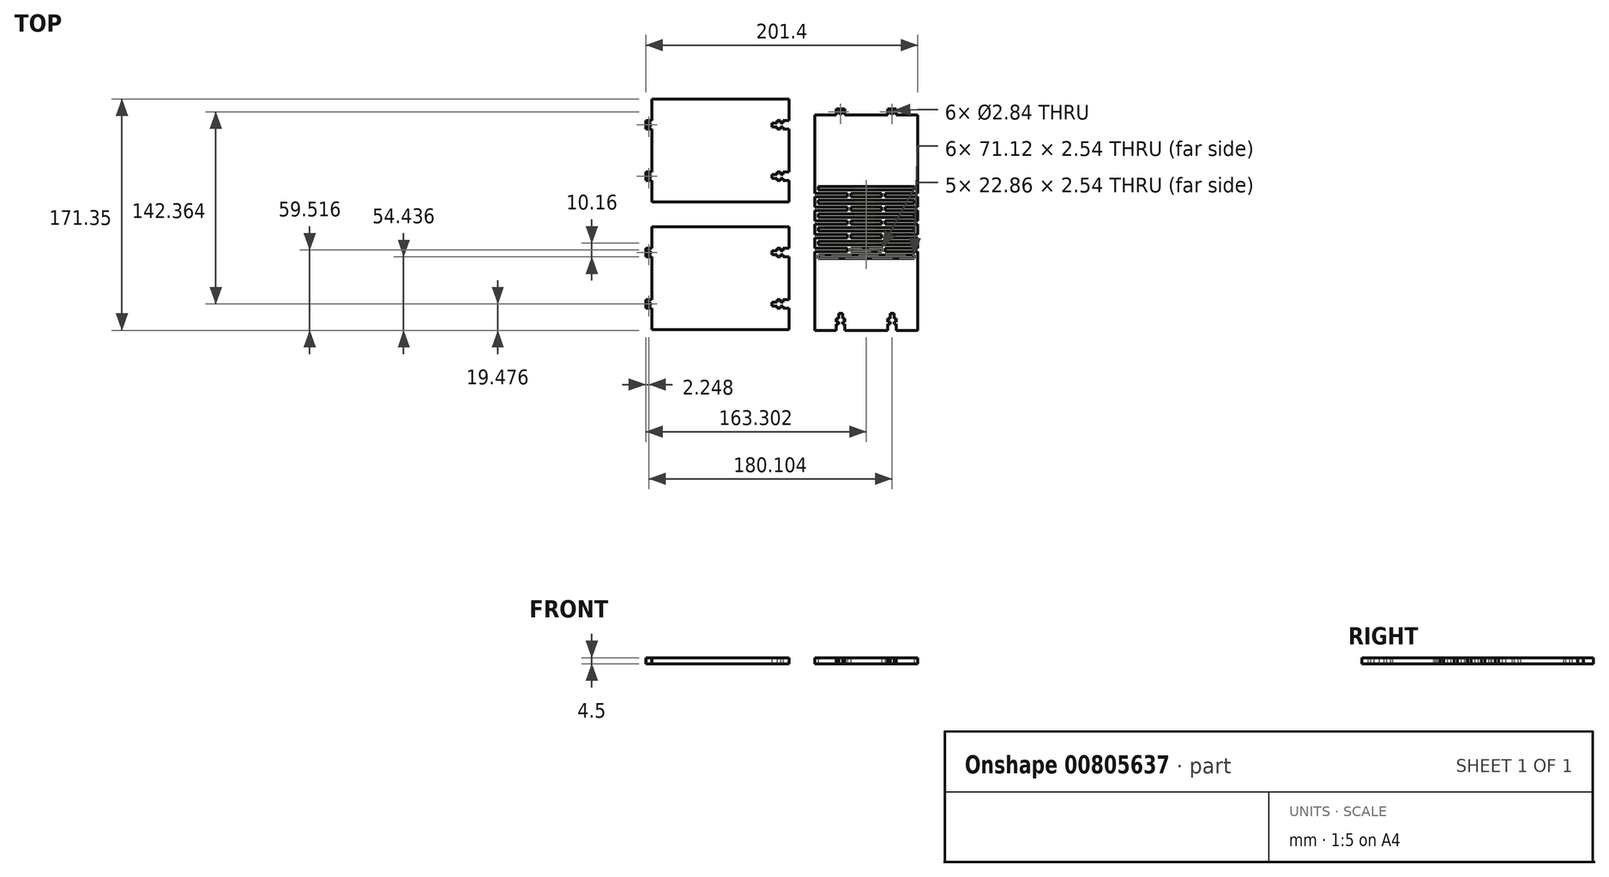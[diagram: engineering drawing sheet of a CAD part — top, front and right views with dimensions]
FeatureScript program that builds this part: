
annotation { "Feature Type Name" : "Feature", "Feature Type Description" : "" }
export const myFeature = defineFeature(function(context is Context, id is Id, definition is map)
    precondition{}
    {
        {
            var Q0;
            Q0=qCreatedBy(makeId("Top.planeOp"),FACE);
            var sketch = newSketch(context, id + "F0", { "sketchPlane" : qUnion([Q0])});
            skLineSegment(sketch, "E0.bottom", {"start": v(-89.07, 43.47) * mm, "end": v(12.53, 43.47) * mm});
            skLineSegment(sketch, "E0.top", {"start": v(-89.07, -32.73) * mm, "end": v(12.53, -32.73) * mm});
            skLineSegment(sketch, "E0.right", {"start": v(12.53, 43.47) * mm, "end": v(12.53, 27.6) * mm});
            skLineSegment(sketch, "E1.bottom", {"start": v(31.63, 31.71) * mm, "end": v(47.5, 31.71) * mm});
            skLineSegment(sketch, "E1.left", {"start": v(31.63, 31.71) * mm, "end": v(31.63, -26.45) * mm});
            skLineSegment(sketch, "E1.right", {"start": v(107.83, 31.71) * mm, "end": v(107.83, -26.45) * mm});
            skLineSegment(sketch, "E2", {"start": v(12.53, -32.73) * mm, "end": v(12.53, -16.86) * mm});
            skLineSegment(sketch, "E3.bottom", {"start": v(6.18, 27.6) * mm, "end": v(3.8, 27.6) * mm});
            skLineSegment(sketch, "E3.top", {"start": v(6.18, 21.24) * mm, "end": v(3.8, 21.24) * mm});
            skLineSegment(sketch, "E3.left", {"start": v(6.18, 27.6) * mm, "end": v(6.18, 25.84) * mm});
            skLineSegment(sketch, "E3.right", {"start": v(3.8, 27.6) * mm, "end": v(3.8, 25.84) * mm});
            skLineSegment(sketch, "E4.0", {"start": v(3.8, 25.84) * mm, "end": v(-0.17, 25.84) * mm});
            skLineSegment(sketch, "E5.0", {"start": v(3.8, 23) * mm, "end": v(-0.17, 23) * mm});
            skLineSegment(sketch, "E6", {"start": v(-0.17, 25.84) * mm, "end": v(-0.17, 23) * mm});
            skPoint(sketch, "E7.start.orphan", {"position": v(6.18, 24.42) * mm});
            skLineSegment(sketch, "E8.trimOffspring", {"start": v(6.18, 23) * mm, "end": v(6.18, 21.24) * mm});
            skLineSegment(sketch, "E9.trimOffspring", {"start": v(3.8, 23) * mm, "end": v(3.8, 21.24) * mm});
            skLineSegment(sketch, "E10", {"start": v(-89.07, 43.47) * mm, "end": v(-89.07, 27.6) * mm});
            skLineSegment(sketch, "E11.0", {"start": v(-89.07, 27.6) * mm, "end": v(-93.57, 27.6) * mm});
            skLineSegment(sketch, "E12.0", {"start": v(-89.07, 21.24) * mm, "end": v(-93.57, 21.24) * mm});
            skLineSegment(sketch, "E13", {"start": v(-93.57, 27.6) * mm, "end": v(-93.57, 21.24) * mm});
            skLineSegment(sketch, "E14.trimOffspring", {"start": v(-89.07, 21.24) * mm, "end": v(-89.07, -10.51) * mm});
            skLineSegment(sketch, "E15.0", {"start": v(12.53, 21.24) * mm, "end": v(7.95, 21.24) * mm});
            skLineSegment(sketch, "E16.0", {"start": v(12.53, 27.6) * mm, "end": v(7.95, 27.6) * mm});
            skLineSegment(sketch, "E17", {"start": v(7.95, 27.6) * mm, "end": v(7.95, 25.84) * mm});
            skLineSegment(sketch, "E18", {"start": v(6.18, 23) * mm, "end": v(7.95, 23) * mm});
            skLineSegment(sketch, "E19", {"start": v(6.18, 25.84) * mm, "end": v(7.95, 25.84) * mm});
            skLineSegment(sketch, "E20.trimOffspring", {"start": v(7.95, 23) * mm, "end": v(7.95, 21.24) * mm});
            skLineSegment(sketch, "E21.MirrorCS", {"start": v(6.18, -16.86) * mm, "end": v(3.8, -16.86) * mm});
            skLineSegment(sketch, "E22.MirrorCS", {"start": v(6.18, -12.26) * mm, "end": v(7.95, -12.26) * mm});
            skLineSegment(sketch, "E23.MirrorCS", {"start": v(6.18, -10.5) * mm, "end": v(3.8, -10.5) * mm});
            skLineSegment(sketch, "E24.MirrorCS", {"start": v(6.18, -15.1) * mm, "end": v(7.95, -15.1) * mm});
            skLineSegment(sketch, "E25.MirrorCS", {"start": v(6.18, -16.86) * mm, "end": v(6.18, -15.1) * mm});
            skLineSegment(sketch, "E26.MirrorCS", {"start": v(7.95, -12.26) * mm, "end": v(7.95, -10.5) * mm});
            skLineSegment(sketch, "E27.MirrorCS", {"start": v(7.95, -16.86) * mm, "end": v(7.95, -15.1) * mm});
            skLineSegment(sketch, "E28.MirrorCS", {"start": v(6.18, -12.26) * mm, "end": v(6.18, -10.5) * mm});
            skLineSegment(sketch, "E29.MirrorCS", {"start": v(3.8, -12.26) * mm, "end": v(3.8, -10.5) * mm});
            skLineSegment(sketch, "E30.MirrorCS", {"start": v(-0.17, -15.1) * mm, "end": v(-0.17, -12.26) * mm});
            skLineSegment(sketch, "E31.MirrorCS", {"start": v(3.8, -15.1) * mm, "end": v(-0.17, -15.1) * mm});
            skLineSegment(sketch, "E32.MirrorCS", {"start": v(3.8, -12.26) * mm, "end": v(-0.17, -12.26) * mm});
            skLineSegment(sketch, "E33.MirrorCS", {"start": v(3.8, -16.86) * mm, "end": v(3.8, -15.1) * mm});
            skLineSegment(sketch, "E34.MirrorCS", {"start": v(-89.07, -10.51) * mm, "end": v(-93.57, -10.51) * mm});
            skPoint(sketch, "E35.MirrorP", {"position": v(6.18, -13.68) * mm});
            skLineSegment(sketch, "E36.MirrorCS", {"start": v(12.53, -16.86) * mm, "end": v(7.95, -16.86) * mm});
            skLineSegment(sketch, "E37.MirrorCS", {"start": v(-89.07, -16.86) * mm, "end": v(-93.57, -16.86) * mm});
            skLineSegment(sketch, "E38.MirrorCS", {"start": v(12.53, -10.5) * mm, "end": v(7.95, -10.5) * mm});
            skLineSegment(sketch, "E39.MirrorCS", {"start": v(-93.57, -16.86) * mm, "end": v(-93.57, -10.51) * mm});
            skLineSegment(sketch, "E40.trimOffspring", {"start": v(12.53, 21.24) * mm, "end": v(12.53, -10.5) * mm});
            skLineSegment(sketch, "E41.trimOffspring", {"start": v(12.53, -16.86) * mm, "end": v(12.53, -32.73) * mm});
            skLineSegment(sketch, "E42.trimOffspring", {"start": v(-89.07, -16.86) * mm, "end": v(-89.07, -32.73) * mm});
            skPoint(sketch, "E43.start.orphan", {"position": v(12.53, 5.37) * mm});
            skPoint(sketch, "E44.MirrorCS.start.orphan", {"position": v(12.53, -127.45) * mm});
            skPoint(sketch, "E45.MirrorCS.end.orphan", {"position": v(12.53, -51.25) * mm});
            skPoint(sketch, "E46.MirrorCS.end.orphan", {"position": v(-89.07, -51.25) * mm});
            skPoint(sketch, "E46.MirrorCS.start.orphan", {"position": v(-89.07, -127.45) * mm});
            skLineSegment(sketch, "E47.MirrorCS", {"start": v(7.95, -71.72) * mm, "end": v(7.95, -73.48) * mm});
            skLineSegment(sketch, "E48.MirrorCS", {"start": v(6.18, -106.98) * mm, "end": v(7.95, -106.98) * mm});
            skLineSegment(sketch, "E49.MirrorCS", {"start": v(7.95, -106.98) * mm, "end": v(7.95, -105.22) * mm});
            skLineSegment(sketch, "E50.MirrorCS", {"start": v(6.18, -71.72) * mm, "end": v(7.95, -71.72) * mm});
            skLineSegment(sketch, "E51.MirrorCS", {"start": v(3.8, -106.98) * mm, "end": v(3.8, -105.23) * mm});
            skLineSegment(sketch, "E52.MirrorCS", {"start": v(6.18, -105.23) * mm, "end": v(3.8, -105.23) * mm});
            skLineSegment(sketch, "E53.MirrorCS", {"start": v(3.8, -71.72) * mm, "end": v(3.8, -73.48) * mm});
            skLineSegment(sketch, "E54.MirrorCS", {"start": v(6.18, -73.48) * mm, "end": v(3.8, -73.48) * mm});
            skLineSegment(sketch, "E55.MirrorCS", {"start": v(6.18, -71.72) * mm, "end": v(6.18, -73.48) * mm});
            skLineSegment(sketch, "E56.MirrorCS", {"start": v(6.18, -106.98) * mm, "end": v(6.18, -105.23) * mm});
            skLineSegment(sketch, "E57.MirrorCS", {"start": v(3.8, -67.13) * mm, "end": v(3.8, -68.88) * mm});
            skLineSegment(sketch, "E58.MirrorCS", {"start": v(7.95, -111.58) * mm, "end": v(7.95, -109.82) * mm});
            skLineSegment(sketch, "E59.MirrorCS", {"start": v(3.8, -111.58) * mm, "end": v(3.8, -109.82) * mm});
            skLineSegment(sketch, "E60.MirrorCS", {"start": v(6.18, -111.58) * mm, "end": v(3.8, -111.58) * mm});
            skLineSegment(sketch, "E61.MirrorCS", {"start": v(6.18, -67.13) * mm, "end": v(6.18, -68.88) * mm});
            skLineSegment(sketch, "E62.MirrorCS", {"start": v(6.18, -67.13) * mm, "end": v(3.8, -67.13) * mm});
            skLineSegment(sketch, "E63.MirrorCS", {"start": v(12.53, -67.12) * mm, "end": v(7.95, -67.12) * mm});
            skLineSegment(sketch, "E64.MirrorCS", {"start": v(6.18, -109.82) * mm, "end": v(7.95, -109.82) * mm});
            skLineSegment(sketch, "E65.MirrorCS", {"start": v(6.18, -111.58) * mm, "end": v(6.18, -109.82) * mm});
            skLineSegment(sketch, "E66.MirrorCS", {"start": v(7.95, -67.12) * mm, "end": v(7.95, -68.88) * mm});
            skLineSegment(sketch, "E67.MirrorCS", {"start": v(6.18, -68.88) * mm, "end": v(7.95, -68.88) * mm});
            skLineSegment(sketch, "E68.MirrorCS", {"start": v(3.8, -109.82) * mm, "end": v(-0.17, -109.82) * mm});
            skLineSegment(sketch, "E69.MirrorCS", {"start": v(3.8, -106.98) * mm, "end": v(-0.17, -106.98) * mm});
            skLineSegment(sketch, "E70.MirrorCS", {"start": v(-89.07, -73.47) * mm, "end": v(-93.57, -73.47) * mm});
            skLineSegment(sketch, "E71.MirrorCS", {"start": v(-93.57, -111.58) * mm, "end": v(-93.57, -105.23) * mm});
            skLineSegment(sketch, "E72.MirrorCS", {"start": v(-93.57, -67.12) * mm, "end": v(-93.57, -73.47) * mm});
            skLineSegment(sketch, "E73.MirrorCS", {"start": v(12.53, -111.58) * mm, "end": v(7.95, -111.58) * mm});
            skLineSegment(sketch, "E74.MirrorCS", {"start": v(3.8, -71.72) * mm, "end": v(-0.17, -71.72) * mm});
            skLineSegment(sketch, "E75.MirrorCS", {"start": v(3.8, -68.88) * mm, "end": v(-0.17, -68.88) * mm});
            skLineSegment(sketch, "E76.MirrorCS", {"start": v(12.53, -105.22) * mm, "end": v(7.95, -105.22) * mm});
            skLineSegment(sketch, "E77.MirrorCS", {"start": v(-89.07, -105.23) * mm, "end": v(-93.57, -105.23) * mm});
            skLineSegment(sketch, "E78.MirrorCS", {"start": v(12.53, -73.48) * mm, "end": v(7.95, -73.48) * mm});
            skLineSegment(sketch, "E79.MirrorCS", {"start": v(-89.07, -67.12) * mm, "end": v(-93.57, -67.12) * mm});
            skLineSegment(sketch, "E80.MirrorCS", {"start": v(-0.17, -68.88) * mm, "end": v(-0.17, -71.72) * mm});
            skLineSegment(sketch, "E81.MirrorCS", {"start": v(-0.17, -109.82) * mm, "end": v(-0.17, -106.98) * mm});
            skLineSegment(sketch, "E82.MirrorCS", {"start": v(-89.07, -111.58) * mm, "end": v(-93.57, -111.58) * mm});
            skLineSegment(sketch, "E83.MirrorCS", {"start": v(12.53, -127.45) * mm, "end": v(12.53, -111.58) * mm});
            skLineSegment(sketch, "E84.MirrorCS", {"start": v(12.53, -51.25) * mm, "end": v(12.53, -67.12) * mm});
            skLineSegment(sketch, "E85.MirrorCS", {"start": v(-89.07, -127.45) * mm, "end": v(-89.07, -111.58) * mm});
            skLineSegment(sketch, "E86.MirrorCS", {"start": v(-89.07, -127.45) * mm, "end": v(12.53, -127.45) * mm});
            skLineSegment(sketch, "E87.MirrorCS", {"start": v(-89.07, -51.25) * mm, "end": v(12.53, -51.25) * mm});
            skPoint(sketch, "E88.MirrorP", {"position": v(6.18, -108.4) * mm});
            skLineSegment(sketch, "E89.MirrorCS", {"start": v(-89.07, -67.12) * mm, "end": v(-89.07, -51.25) * mm});
            skLineSegment(sketch, "E90.MirrorCS", {"start": v(-89.07, -105.23) * mm, "end": v(-89.07, -73.47) * mm});
            skPoint(sketch, "E91.MirrorP", {"position": v(6.18, -70.3) * mm});
            skLineSegment(sketch, "E92.MirrorCS", {"start": v(12.53, -105.22) * mm, "end": v(12.53, -73.48) * mm});
            skLineSegment(sketch, "E93.MirrorCS", {"start": v(12.53, -67.12) * mm, "end": v(12.53, -51.25) * mm});
            skPoint(sketch, "E94.MirrorP", {"position": v(12.53, -89.35) * mm});
            skCircle(sketch, "E95", {"center": v(-91.32, 24.42) * mm, "radius": 1.42 * mm});
            skPoint(sketch, "E95.centerSnap0", {"position": v(-91.32, 27.6) * mm});
            skPoint(sketch, "E95.centerSnap1", {"position": v(-93.57, 24.42) * mm});
            skCircle(sketch, "E96.MirrorC", {"center": v(-91.32, -13.69) * mm, "radius": 1.42 * mm});
            skCircle(sketch, "E97.MirrorC", {"center": v(-91.32, -108.4) * mm, "radius": 1.42 * mm});
            skCircle(sketch, "E98.MirrorC", {"center": v(-91.32, -70.3) * mm, "radius": 1.42 * mm});
            skLineSegment(sketch, "E99", {"start": v(53.86, 31.71) * mm, "end": v(85.6, 31.71) * mm});
            skLineSegment(sketch, "E100.top", {"start": v(47.5, 36.2) * mm, "end": v(53.86, 36.2) * mm});
            skLineSegment(sketch, "E100.left", {"start": v(47.5, 31.71) * mm, "end": v(47.5, 36.2) * mm});
            skLineSegment(sketch, "E100.right", {"start": v(53.86, 31.71) * mm, "end": v(53.86, 36.2) * mm});
            skLineSegment(sketch, "E101.MirrorCS", {"start": v(91.96, 36.2) * mm, "end": v(85.6, 36.2) * mm});
            skLineSegment(sketch, "E102.MirrorCS", {"start": v(91.96, 31.71) * mm, "end": v(91.96, 36.2) * mm});
            skLineSegment(sketch, "E103.MirrorCS", {"start": v(85.6, 31.71) * mm, "end": v(85.6, 36.2) * mm});
            skCircle(sketch, "E104", {"center": v(50.68, 33.96) * mm, "radius": 1.42 * mm});
            skPoint(sketch, "E104.centerSnap0", {"position": v(50.68, 36.2) * mm});
            skPoint(sketch, "E105.start.orphan", {"position": v(47.5, 33.96) * mm});
            skPoint(sketch, "E106.trimOffspring.end.orphan", {"position": v(53.86, 33.96) * mm});
            skPoint(sketch, "E107.orphan", {"position": v(50.68, 31.71) * mm});
            skLineSegment(sketch, "E108.trimOffspring", {"start": v(91.96, 31.71) * mm, "end": v(107.83, 31.71) * mm});
            skPoint(sketch, "E109.end.orphan", {"position": v(69.73, 31.71) * mm});
            skPoint(sketch, "E110.end.orphan", {"position": v(-89.07, 5.37) * mm});
            skLineSegment(sketch, "E111", {"start": v(31.63, 31.71) * mm, "end": v(31.63, -21.37) * mm});
            skLineSegment(sketch, "E112", {"start": v(34.17, -21.37) * mm, "end": v(69.73, -21.37) * mm});
            skLineSegment(sketch, "E113", {"start": v(69.73, 31.71) * mm, "end": v(69.73, -127.88) * mm});
            skLineSegment(sketch, "E114.0", {"start": v(34.17, -23.91) * mm, "end": v(55.76, -23.91) * mm});
            skLineSegment(sketch, "E115.0", {"start": v(31.63, -26.45) * mm, "end": v(55.76, -26.45) * mm});
            skLineSegment(sketch, "E116", {"start": v(34.17, -21.37) * mm, "end": v(34.17, -23.91) * mm});
            skPoint(sketch, "E117.orphan", {"position": v(31.63, -23.91) * mm});
            skLineSegment(sketch, "E118.trimOffspring", {"start": v(55.87, -23.91) * mm, "end": v(69.73, -23.91) * mm});
            skLineSegment(sketch, "E119.trimOffspring", {"start": v(58.3, -26.45) * mm, "end": v(69.73, -26.45) * mm});
            skLineSegment(sketch, "E120.MirrorCS", {"start": v(107.83, 31.71) * mm, "end": v(107.83, -21.37) * mm});
            skPoint(sketch, "E121.MirrorP", {"position": v(107.83, -23.91) * mm});
            skLineSegment(sketch, "E122.0", {"start": v(31.63, -29) * mm, "end": v(55.76, -29) * mm});
            skLineSegment(sketch, "E123", {"start": v(58.3, -29) * mm, "end": v(69.73, -29) * mm});
            skLineSegment(sketch, "E124", {"start": v(55.76, -23.91) * mm, "end": v(55.87, -23.91) * mm});
            skLineSegment(sketch, "E125", {"start": v(55.76, -26.45) * mm, "end": v(55.76, -29) * mm});
            skLineSegment(sketch, "E126", {"start": v(58.3, -26.45) * mm, "end": v(58.3, -29) * mm});
            skLineSegment(sketch, "E127.trimOffspring", {"start": v(31.63, -29) * mm, "end": v(31.63, -36.61) * mm});
            skPoint(sketch, "E128.MirrorCS.end.orphan", {"position": v(69.73, -26.45) * mm});
            skPoint(sketch, "E129.MirrorCS.end.orphan", {"position": v(69.73, -23.91) * mm});
            skPoint(sketch, "E130.MirrorCS.end.orphan", {"position": v(81.16, -26.45) * mm});
            skPoint(sketch, "E130.MirrorCS.start.orphan", {"position": v(83.6, -23.91) * mm});
            skPoint(sketch, "E131.MirrorCS.end.orphan", {"position": v(83.7, -26.45) * mm});
            skPoint(sketch, "E131.MirrorCS.start.orphan", {"position": v(107.83, -26.45) * mm});
            skPoint(sketch, "E132.MirrorCS.end.orphan", {"position": v(83.7, -23.91) * mm});
            skPoint(sketch, "E133.MirrorCS.end.orphan", {"position": v(69.73, -21.37) * mm});
            skPoint(sketch, "E134.MirrorCS.end.orphan", {"position": v(105.3, -23.91) * mm});
            skPoint(sketch, "E134.MirrorCS.start.orphan", {"position": v(105.3, -21.37) * mm});
            skLineSegment(sketch, "E135.0", {"start": v(34.17, -31.53) * mm, "end": v(55.76, -31.53) * mm});
            skLineSegment(sketch, "E136", {"start": v(55.76, -31.53) * mm, "end": v(69.73, -31.53) * mm});
            skLineSegment(sketch, "E137.MirrorCS", {"start": v(83.7, -26.45) * mm, "end": v(83.7, -29) * mm});
            skLineSegment(sketch, "E138.MirrorCS", {"start": v(105.3, -21.37) * mm, "end": v(105.3, -23.91) * mm});
            skLineSegment(sketch, "E139.MirrorCS", {"start": v(81.16, -26.45) * mm, "end": v(81.16, -29) * mm});
            skLineSegment(sketch, "E140.MirrorCS", {"start": v(83.7, -23.91) * mm, "end": v(83.6, -23.91) * mm});
            skLineSegment(sketch, "E141.MirrorCS", {"start": v(105.3, -23.91) * mm, "end": v(83.7, -23.91) * mm});
            skLineSegment(sketch, "E142.MirrorCS", {"start": v(81.16, -29) * mm, "end": v(69.73, -29) * mm});
            skLineSegment(sketch, "E143.MirrorCS", {"start": v(107.83, -26.45) * mm, "end": v(83.7, -26.45) * mm});
            skLineSegment(sketch, "E144.MirrorCS", {"start": v(83.7, -31.53) * mm, "end": v(69.73, -31.53) * mm});
            skLineSegment(sketch, "E145.MirrorCS", {"start": v(83.6, -23.91) * mm, "end": v(69.73, -23.91) * mm});
            skLineSegment(sketch, "E146.MirrorCS", {"start": v(81.16, -26.45) * mm, "end": v(69.73, -26.45) * mm});
            skLineSegment(sketch, "E147.MirrorCS", {"start": v(107.83, -29) * mm, "end": v(107.83, -36.61) * mm});
            skLineSegment(sketch, "E148.MirrorCS", {"start": v(107.83, -29) * mm, "end": v(83.7, -29) * mm});
            skLineSegment(sketch, "E149.MirrorCS", {"start": v(105.3, -31.53) * mm, "end": v(83.7, -31.53) * mm});
            skLineSegment(sketch, "E150.MirrorCS", {"start": v(105.3, -21.37) * mm, "end": v(69.73, -21.37) * mm});
            skLineSegment(sketch, "E151.0.1.0", {"start": v(55.87, -34.07) * mm, "end": v(69.73, -34.07) * mm});
            skPoint(sketch, "E151.0.1.1", {"position": v(107.83, -34.07) * mm});
            skLineSegment(sketch, "E151.0.1.2", {"start": v(105.3, -34.07) * mm, "end": v(83.7, -34.07) * mm});
            skLineSegment(sketch, "E151.0.1.3", {"start": v(31.63, -39.15) * mm, "end": v(55.76, -39.15) * mm});
            skPoint(sketch, "E151.0.1.4", {"position": v(83.7, -34.07) * mm});
            skLineSegment(sketch, "E151.0.1.5", {"start": v(31.63, -36.61) * mm, "end": v(55.76, -36.61) * mm});
            skPoint(sketch, "E151.0.1.6", {"position": v(105.3, -34.07) * mm});
            skLineSegment(sketch, "E151.0.1.7", {"start": v(58.3, -36.61) * mm, "end": v(69.73, -36.61) * mm});
            skLineSegment(sketch, "E151.0.1.8", {"start": v(83.7, -41.7) * mm, "end": v(69.73, -41.7) * mm});
            skLineSegment(sketch, "E151.0.1.9", {"start": v(58.3, -39.15) * mm, "end": v(69.73, -39.15) * mm});
            skPoint(sketch, "E151.0.1.10", {"position": v(105.3, -31.53) * mm});
            skLineSegment(sketch, "E151.0.1.11", {"start": v(81.16, -39.15) * mm, "end": v(69.73, -39.15) * mm});
            skLineSegment(sketch, "E151.0.1.12", {"start": v(107.83, -36.61) * mm, "end": v(83.7, -36.61) * mm});
            skLineSegment(sketch, "E151.0.1.13", {"start": v(34.17, -34.07) * mm, "end": v(55.76, -34.07) * mm});
            skLineSegment(sketch, "E151.0.1.14", {"start": v(105.3, -31.53) * mm, "end": v(69.73, -31.53) * mm});
            skPoint(sketch, "E151.0.1.15", {"position": v(107.83, -36.61) * mm});
            skLineSegment(sketch, "E151.0.1.16", {"start": v(55.76, -41.7) * mm, "end": v(69.73, -41.7) * mm});
            skLineSegment(sketch, "E151.0.1.17", {"start": v(105.3, -41.7) * mm, "end": v(83.7, -41.7) * mm});
            skPoint(sketch, "E151.0.1.18", {"position": v(83.7, -36.61) * mm});
            skLineSegment(sketch, "E151.0.1.19", {"start": v(34.17, -31.53) * mm, "end": v(69.73, -31.53) * mm});
            skPoint(sketch, "E151.0.1.20", {"position": v(83.6, -34.07) * mm});
            skLineSegment(sketch, "E151.0.1.21", {"start": v(34.17, -41.7) * mm, "end": v(55.76, -41.7) * mm});
            skLineSegment(sketch, "E151.0.1.22", {"start": v(107.83, -39.15) * mm, "end": v(83.7, -39.15) * mm});
            skPoint(sketch, "E151.0.1.23", {"position": v(81.16, -36.61) * mm});
            skLineSegment(sketch, "E151.0.1.24", {"start": v(81.16, -36.61) * mm, "end": v(69.73, -36.61) * mm});
            skLineSegment(sketch, "E151.0.1.25", {"start": v(83.6, -34.07) * mm, "end": v(69.73, -34.07) * mm});
            skPoint(sketch, "E151.0.1.26", {"position": v(31.63, -34.07) * mm});
            skLineSegment(sketch, "E151.0.1.27", {"start": v(105.3, -34.07) * mm, "end": v(83.7, -34.07) * mm});
            skPoint(sketch, "E151.0.1.28", {"position": v(69.73, -31.53) * mm});
            skPoint(sketch, "E151.0.1.29", {"position": v(69.73, -36.61) * mm});
            skPoint(sketch, "E151.0.1.30", {"position": v(69.73, -34.07) * mm});
            skLineSegment(sketch, "E151.0.1.31", {"start": v(34.17, -34.07) * mm, "end": v(55.76, -34.07) * mm});
            skPoint(sketch, "E151.0.1.32", {"position": v(107.83, -34.07) * mm});
            skPoint(sketch, "E151.0.1.33", {"position": v(69.73, -31.53) * mm});
            skLineSegment(sketch, "E151.0.1.34", {"start": v(34.17, -31.53) * mm, "end": v(34.17, -34.07) * mm});
            skLineSegment(sketch, "E151.0.1.35", {"start": v(81.16, -36.61) * mm, "end": v(81.16, -39.15) * mm});
            skLineSegment(sketch, "E151.0.1.36", {"start": v(58.3, -36.61) * mm, "end": v(58.3, -39.15) * mm});
            skPoint(sketch, "E151.0.1.37", {"position": v(69.73, -34.07) * mm});
            skLineSegment(sketch, "E151.0.1.38", {"start": v(55.76, -36.61) * mm, "end": v(55.76, -39.15) * mm});
            skPoint(sketch, "E151.0.1.39", {"position": v(69.73, -36.61) * mm});
            skLineSegment(sketch, "E151.0.1.40", {"start": v(55.76, -34.07) * mm, "end": v(55.87, -34.07) * mm});
            skLineSegment(sketch, "E151.0.1.41", {"start": v(105.3, -31.53) * mm, "end": v(105.3, -34.07) * mm});
            skLineSegment(sketch, "E151.0.1.42", {"start": v(83.7, -34.07) * mm, "end": v(83.6, -34.07) * mm});
            skLineSegment(sketch, "E151.0.1.43", {"start": v(83.7, -36.61) * mm, "end": v(83.7, -39.15) * mm});
            skLineSegment(sketch, "E151.0.2.0", {"start": v(55.87, -44.23) * mm, "end": v(69.73, -44.23) * mm});
            skPoint(sketch, "E151.0.2.1", {"position": v(107.83, -44.23) * mm});
            skLineSegment(sketch, "E151.0.2.2", {"start": v(105.3, -44.23) * mm, "end": v(83.7, -44.23) * mm});
            skLineSegment(sketch, "E151.0.2.3", {"start": v(31.63, -49.31) * mm, "end": v(55.76, -49.31) * mm});
            skPoint(sketch, "E151.0.2.4", {"position": v(83.7, -44.23) * mm});
            skLineSegment(sketch, "E151.0.2.5", {"start": v(31.63, -46.77) * mm, "end": v(55.76, -46.77) * mm});
            skPoint(sketch, "E151.0.2.6", {"position": v(105.3, -44.23) * mm});
            skLineSegment(sketch, "E151.0.2.7", {"start": v(58.3, -46.77) * mm, "end": v(69.73, -46.77) * mm});
            skLineSegment(sketch, "E151.0.2.8", {"start": v(83.7, -51.85) * mm, "end": v(69.73, -51.85) * mm});
            skLineSegment(sketch, "E151.0.2.9", {"start": v(58.3, -49.31) * mm, "end": v(69.73, -49.31) * mm});
            skPoint(sketch, "E151.0.2.10", {"position": v(105.3, -41.7) * mm});
            skLineSegment(sketch, "E151.0.2.11", {"start": v(81.16, -49.31) * mm, "end": v(69.73, -49.31) * mm});
            skLineSegment(sketch, "E151.0.2.12", {"start": v(107.83, -46.77) * mm, "end": v(83.7, -46.77) * mm});
            skLineSegment(sketch, "E151.0.2.13", {"start": v(34.17, -44.23) * mm, "end": v(55.76, -44.23) * mm});
            skLineSegment(sketch, "E151.0.2.14", {"start": v(105.3, -41.7) * mm, "end": v(69.73, -41.7) * mm});
            skPoint(sketch, "E151.0.2.15", {"position": v(107.83, -46.77) * mm});
            skLineSegment(sketch, "E151.0.2.16", {"start": v(55.76, -51.85) * mm, "end": v(69.73, -51.85) * mm});
            skLineSegment(sketch, "E151.0.2.17", {"start": v(105.3, -51.85) * mm, "end": v(83.7, -51.85) * mm});
            skPoint(sketch, "E151.0.2.18", {"position": v(83.7, -46.77) * mm});
            skLineSegment(sketch, "E151.0.2.19", {"start": v(34.17, -41.7) * mm, "end": v(69.73, -41.7) * mm});
            skPoint(sketch, "E151.0.2.20", {"position": v(83.6, -44.23) * mm});
            skLineSegment(sketch, "E151.0.2.21", {"start": v(34.17, -51.85) * mm, "end": v(55.76, -51.85) * mm});
            skLineSegment(sketch, "E151.0.2.22", {"start": v(107.83, -49.31) * mm, "end": v(83.7, -49.31) * mm});
            skPoint(sketch, "E151.0.2.23", {"position": v(81.16, -46.77) * mm});
            skLineSegment(sketch, "E151.0.2.24", {"start": v(81.16, -46.77) * mm, "end": v(69.73, -46.77) * mm});
            skLineSegment(sketch, "E151.0.2.25", {"start": v(83.6, -44.23) * mm, "end": v(69.73, -44.23) * mm});
            skPoint(sketch, "E151.0.2.26", {"position": v(31.63, -44.23) * mm});
            skLineSegment(sketch, "E151.0.2.27", {"start": v(105.3, -44.23) * mm, "end": v(83.7, -44.23) * mm});
            skPoint(sketch, "E151.0.2.28", {"position": v(69.73, -41.7) * mm});
            skPoint(sketch, "E151.0.2.29", {"position": v(69.73, -46.77) * mm});
            skPoint(sketch, "E151.0.2.30", {"position": v(69.73, -44.23) * mm});
            skLineSegment(sketch, "E151.0.2.31", {"start": v(34.17, -44.23) * mm, "end": v(55.76, -44.23) * mm});
            skPoint(sketch, "E151.0.2.32", {"position": v(107.83, -44.23) * mm});
            skPoint(sketch, "E151.0.2.33", {"position": v(69.73, -41.7) * mm});
            skLineSegment(sketch, "E151.0.2.34", {"start": v(34.17, -41.7) * mm, "end": v(34.17, -44.23) * mm});
            skLineSegment(sketch, "E151.0.2.35", {"start": v(81.16, -46.77) * mm, "end": v(81.16, -49.31) * mm});
            skLineSegment(sketch, "E151.0.2.36", {"start": v(58.3, -46.77) * mm, "end": v(58.3, -49.31) * mm});
            skPoint(sketch, "E151.0.2.37", {"position": v(69.73, -44.23) * mm});
            skLineSegment(sketch, "E151.0.2.38", {"start": v(55.76, -46.77) * mm, "end": v(55.76, -49.31) * mm});
            skPoint(sketch, "E151.0.2.39", {"position": v(69.73, -46.77) * mm});
            skLineSegment(sketch, "E151.0.2.40", {"start": v(55.76, -44.23) * mm, "end": v(55.87, -44.23) * mm});
            skLineSegment(sketch, "E151.0.2.41", {"start": v(105.3, -41.7) * mm, "end": v(105.3, -44.23) * mm});
            skLineSegment(sketch, "E151.0.2.42", {"start": v(83.7, -44.23) * mm, "end": v(83.6, -44.23) * mm});
            skLineSegment(sketch, "E151.0.2.43", {"start": v(83.7, -46.77) * mm, "end": v(83.7, -49.31) * mm});
            skLineSegment(sketch, "E151.0.3.0", {"start": v(55.87, -54.4) * mm, "end": v(69.73, -54.4) * mm});
            skPoint(sketch, "E151.0.3.1", {"position": v(107.83, -54.4) * mm});
            skLineSegment(sketch, "E151.0.3.2", {"start": v(105.3, -54.4) * mm, "end": v(83.7, -54.4) * mm});
            skLineSegment(sketch, "E151.0.3.3", {"start": v(31.63, -59.47) * mm, "end": v(55.76, -59.47) * mm});
            skPoint(sketch, "E151.0.3.4", {"position": v(83.7, -54.4) * mm});
            skLineSegment(sketch, "E151.0.3.5", {"start": v(31.63, -56.93) * mm, "end": v(55.76, -56.93) * mm});
            skPoint(sketch, "E151.0.3.6", {"position": v(105.3, -54.4) * mm});
            skLineSegment(sketch, "E151.0.3.7", {"start": v(58.3, -56.93) * mm, "end": v(69.73, -56.93) * mm});
            skLineSegment(sketch, "E151.0.3.8", {"start": v(83.7, -62.01) * mm, "end": v(69.73, -62.01) * mm});
            skLineSegment(sketch, "E151.0.3.9", {"start": v(58.3, -59.47) * mm, "end": v(69.73, -59.47) * mm});
            skPoint(sketch, "E151.0.3.10", {"position": v(105.3, -51.85) * mm});
            skLineSegment(sketch, "E151.0.3.11", {"start": v(81.16, -59.47) * mm, "end": v(69.73, -59.47) * mm});
            skLineSegment(sketch, "E151.0.3.12", {"start": v(107.83, -56.93) * mm, "end": v(83.7, -56.93) * mm});
            skLineSegment(sketch, "E151.0.3.13", {"start": v(34.17, -54.4) * mm, "end": v(55.76, -54.4) * mm});
            skLineSegment(sketch, "E151.0.3.14", {"start": v(105.3, -51.85) * mm, "end": v(69.73, -51.85) * mm});
            skPoint(sketch, "E151.0.3.15", {"position": v(107.83, -56.93) * mm});
            skLineSegment(sketch, "E151.0.3.16", {"start": v(55.76, -62.01) * mm, "end": v(69.73, -62.01) * mm});
            skLineSegment(sketch, "E151.0.3.17", {"start": v(105.3, -62.01) * mm, "end": v(83.7, -62.01) * mm});
            skPoint(sketch, "E151.0.3.18", {"position": v(83.7, -56.93) * mm});
            skLineSegment(sketch, "E151.0.3.19", {"start": v(34.17, -51.85) * mm, "end": v(69.73, -51.85) * mm});
            skPoint(sketch, "E151.0.3.20", {"position": v(83.6, -54.4) * mm});
            skLineSegment(sketch, "E151.0.3.21", {"start": v(34.17, -62.01) * mm, "end": v(55.76, -62.01) * mm});
            skLineSegment(sketch, "E151.0.3.22", {"start": v(107.83, -59.47) * mm, "end": v(83.7, -59.47) * mm});
            skPoint(sketch, "E151.0.3.23", {"position": v(81.16, -56.93) * mm});
            skLineSegment(sketch, "E151.0.3.24", {"start": v(81.16, -56.93) * mm, "end": v(69.73, -56.93) * mm});
            skLineSegment(sketch, "E151.0.3.25", {"start": v(83.6, -54.4) * mm, "end": v(69.73, -54.4) * mm});
            skPoint(sketch, "E151.0.3.26", {"position": v(31.63, -54.4) * mm});
            skLineSegment(sketch, "E151.0.3.27", {"start": v(105.3, -54.4) * mm, "end": v(83.7, -54.4) * mm});
            skPoint(sketch, "E151.0.3.28", {"position": v(69.73, -51.85) * mm});
            skPoint(sketch, "E151.0.3.29", {"position": v(69.73, -56.93) * mm});
            skPoint(sketch, "E151.0.3.30", {"position": v(69.73, -54.4) * mm});
            skLineSegment(sketch, "E151.0.3.31", {"start": v(34.17, -54.4) * mm, "end": v(55.76, -54.4) * mm});
            skPoint(sketch, "E151.0.3.32", {"position": v(107.83, -54.4) * mm});
            skPoint(sketch, "E151.0.3.33", {"position": v(69.73, -51.85) * mm});
            skLineSegment(sketch, "E151.0.3.34", {"start": v(34.17, -51.85) * mm, "end": v(34.17, -54.4) * mm});
            skLineSegment(sketch, "E151.0.3.35", {"start": v(81.16, -56.93) * mm, "end": v(81.16, -59.47) * mm});
            skLineSegment(sketch, "E151.0.3.36", {"start": v(58.3, -56.93) * mm, "end": v(58.3, -59.47) * mm});
            skPoint(sketch, "E151.0.3.37", {"position": v(69.73, -54.4) * mm});
            skLineSegment(sketch, "E151.0.3.38", {"start": v(55.76, -56.93) * mm, "end": v(55.76, -59.47) * mm});
            skPoint(sketch, "E151.0.3.39", {"position": v(69.73, -56.93) * mm});
            skLineSegment(sketch, "E151.0.3.40", {"start": v(55.76, -54.4) * mm, "end": v(55.87, -54.4) * mm});
            skLineSegment(sketch, "E151.0.3.41", {"start": v(105.3, -51.85) * mm, "end": v(105.3, -54.4) * mm});
            skLineSegment(sketch, "E151.0.3.42", {"start": v(83.7, -54.4) * mm, "end": v(83.6, -54.4) * mm});
            skLineSegment(sketch, "E151.0.3.43", {"start": v(83.7, -56.93) * mm, "end": v(83.7, -59.47) * mm});
            skLineSegment(sketch, "E151.0.4.0", {"start": v(55.87, -64.55) * mm, "end": v(69.73, -64.55) * mm});
            skPoint(sketch, "E151.0.4.1", {"position": v(107.83, -64.55) * mm});
            skLineSegment(sketch, "E151.0.4.2", {"start": v(105.3, -64.55) * mm, "end": v(83.7, -64.55) * mm});
            skLineSegment(sketch, "E151.0.4.3", {"start": v(31.63, -69.63) * mm, "end": v(55.76, -69.63) * mm});
            skPoint(sketch, "E151.0.4.4", {"position": v(83.7, -64.55) * mm});
            skLineSegment(sketch, "E151.0.4.5", {"start": v(31.63, -67.1) * mm, "end": v(55.76, -67.1) * mm});
            skPoint(sketch, "E151.0.4.6", {"position": v(105.3, -64.55) * mm});
            skLineSegment(sketch, "E151.0.4.7", {"start": v(58.3, -67.1) * mm, "end": v(69.73, -67.1) * mm});
            skLineSegment(sketch, "E151.0.4.8", {"start": v(83.7, -72.17) * mm, "end": v(69.73, -72.17) * mm});
            skLineSegment(sketch, "E151.0.4.9", {"start": v(58.3, -69.63) * mm, "end": v(69.73, -69.63) * mm});
            skPoint(sketch, "E151.0.4.10", {"position": v(105.3, -62.01) * mm});
            skLineSegment(sketch, "E151.0.4.11", {"start": v(81.16, -69.63) * mm, "end": v(69.73, -69.63) * mm});
            skLineSegment(sketch, "E151.0.4.12", {"start": v(107.83, -67.1) * mm, "end": v(83.7, -67.1) * mm});
            skLineSegment(sketch, "E151.0.4.13", {"start": v(34.17, -64.55) * mm, "end": v(55.76, -64.55) * mm});
            skLineSegment(sketch, "E151.0.4.14", {"start": v(105.3, -62.01) * mm, "end": v(69.73, -62.01) * mm});
            skPoint(sketch, "E151.0.4.15", {"position": v(107.83, -67.1) * mm});
            skLineSegment(sketch, "E151.0.4.16", {"start": v(55.76, -72.17) * mm, "end": v(69.73, -72.17) * mm});
            skLineSegment(sketch, "E151.0.4.17", {"start": v(105.3, -72.17) * mm, "end": v(83.7, -72.17) * mm});
            skPoint(sketch, "E151.0.4.18", {"position": v(83.7, -67.1) * mm});
            skLineSegment(sketch, "E151.0.4.19", {"start": v(34.17, -62.01) * mm, "end": v(69.73, -62.01) * mm});
            skPoint(sketch, "E151.0.4.20", {"position": v(83.6, -64.55) * mm});
            skLineSegment(sketch, "E151.0.4.21", {"start": v(34.17, -72.17) * mm, "end": v(55.76, -72.17) * mm});
            skLineSegment(sketch, "E151.0.4.22", {"start": v(107.83, -69.63) * mm, "end": v(83.7, -69.63) * mm});
            skPoint(sketch, "E151.0.4.23", {"position": v(81.16, -67.1) * mm});
            skLineSegment(sketch, "E151.0.4.24", {"start": v(81.16, -67.1) * mm, "end": v(69.73, -67.1) * mm});
            skLineSegment(sketch, "E151.0.4.25", {"start": v(83.6, -64.55) * mm, "end": v(69.73, -64.55) * mm});
            skPoint(sketch, "E151.0.4.26", {"position": v(31.63, -64.55) * mm});
            skLineSegment(sketch, "E151.0.4.27", {"start": v(105.3, -64.55) * mm, "end": v(83.7, -64.55) * mm});
            skPoint(sketch, "E151.0.4.28", {"position": v(69.73, -62.01) * mm});
            skPoint(sketch, "E151.0.4.29", {"position": v(69.73, -67.1) * mm});
            skPoint(sketch, "E151.0.4.30", {"position": v(69.73, -64.55) * mm});
            skLineSegment(sketch, "E151.0.4.31", {"start": v(34.17, -64.55) * mm, "end": v(55.76, -64.55) * mm});
            skPoint(sketch, "E151.0.4.32", {"position": v(107.83, -64.55) * mm});
            skPoint(sketch, "E151.0.4.33", {"position": v(69.73, -62.01) * mm});
            skLineSegment(sketch, "E151.0.4.34", {"start": v(34.17, -62.01) * mm, "end": v(34.17, -64.55) * mm});
            skLineSegment(sketch, "E151.0.4.35", {"start": v(81.16, -67.1) * mm, "end": v(81.16, -69.63) * mm});
            skLineSegment(sketch, "E151.0.4.36", {"start": v(58.3, -67.1) * mm, "end": v(58.3, -69.63) * mm});
            skPoint(sketch, "E151.0.4.37", {"position": v(69.73, -64.55) * mm});
            skLineSegment(sketch, "E151.0.4.38", {"start": v(55.76, -67.1) * mm, "end": v(55.76, -69.63) * mm});
            skPoint(sketch, "E151.0.4.39", {"position": v(69.73, -67.1) * mm});
            skLineSegment(sketch, "E151.0.4.40", {"start": v(55.76, -64.55) * mm, "end": v(55.87, -64.55) * mm});
            skLineSegment(sketch, "E151.0.4.41", {"start": v(105.3, -62.01) * mm, "end": v(105.3, -64.55) * mm});
            skLineSegment(sketch, "E151.0.4.42", {"start": v(83.7, -64.55) * mm, "end": v(83.6, -64.55) * mm});
            skLineSegment(sketch, "E151.0.4.43", {"start": v(83.7, -67.1) * mm, "end": v(83.7, -69.63) * mm});
            skLineSegment(sketch, "E151.direction1", {"start": v(34.17, -31.53) * mm, "end": v(57.03, -31.53) * mm, "construction": true});
            skLineSegment(sketch, "E151.direction2", {"start": v(31.63, -31.53) * mm, "end": v(31.63, -36.61) * mm, "construction": true});
            skLineSegment(sketch, "E152.trimOffspring", {"start": v(31.63, -39.15) * mm, "end": v(31.63, -41.7) * mm, "construction": true});
            skLineSegment(sketch, "E153.trimOffspring", {"start": v(31.63, -39.15) * mm, "end": v(31.63, -46.77) * mm});
            skLineSegment(sketch, "E154.trimOffspring", {"start": v(31.63, -49.31) * mm, "end": v(31.63, -56.93) * mm});
            skPoint(sketch, "E155.orphan", {"position": v(31.63, -51.85) * mm});
            skLineSegment(sketch, "E156.trimOffspring", {"start": v(31.63, -59.47) * mm, "end": v(31.63, -67.1) * mm});
            skPoint(sketch, "E157.orphan", {"position": v(31.63, -62.01) * mm});
            skLineSegment(sketch, "E158.trimOffspring", {"start": v(31.63, -69.63) * mm, "end": v(31.63, -127.88) * mm});
            skPoint(sketch, "E159.orphan", {"position": v(107.83, -31.53) * mm});
            skLineSegment(sketch, "E160.trimOffspring", {"start": v(107.83, -39.15) * mm, "end": v(107.83, -46.77) * mm});
            skPoint(sketch, "E161.orphan", {"position": v(107.83, -41.7) * mm});
            skPoint(sketch, "E162.orphan", {"position": v(107.83, -51.85) * mm});
            skLineSegment(sketch, "E163.trimOffspring", {"start": v(107.83, -49.31) * mm, "end": v(107.83, -56.93) * mm});
            skLineSegment(sketch, "E164.trimOffspring", {"start": v(107.83, -59.47) * mm, "end": v(107.83, -67.1) * mm});
            skPoint(sketch, "E165.orphan", {"position": v(107.83, -62.01) * mm});
            skLineSegment(sketch, "E166.trimOffspring", {"start": v(107.83, -69.63) * mm, "end": v(107.83, -127.88) * mm});
            skLineSegment(sketch, "E167.0", {"start": v(34.17, -74.71) * mm, "end": v(55.76, -74.71) * mm});
            skLineSegment(sketch, "E168", {"start": v(55.76, -74.71) * mm, "end": v(105.3, -74.71) * mm});
            skPoint(sketch, "E169.endSnap0", {"position": v(81.8, -74.71) * mm});
            skLineSegment(sketch, "E170.trimOffspring", {"start": v(107.73, -72.17) * mm, "end": v(107.73, -74.71) * mm});
            skPoint(sketch, "E171.orphan", {"position": v(107.83, -72.17) * mm});
            skPoint(sketch, "E172.orphan", {"position": v(107.83, -74.71) * mm});
            skPoint(sketch, "E173.orphan", {"position": v(31.63, -72.17) * mm});
            skLineSegment(sketch, "E174.trimOffspring", {"start": v(34.17, -72.17) * mm, "end": v(34.17, -74.71) * mm});
            skLineSegment(sketch, "E175", {"start": v(31.63, -127.88) * mm, "end": v(47.5, -127.88) * mm});
            skLineSegment(sketch, "E176", {"start": v(105.3, -72.17) * mm, "end": v(105.3, -74.71) * mm});
            skCircle(sketch, "E177", {"center": v(88.78, 33.96) * mm, "radius": 1.42 * mm});
            skPoint(sketch, "E178.start.orphan", {"position": v(85.6, 33.96) * mm});
            skPoint(sketch, "E179.trimOffspring.end.orphan", {"position": v(91.96, 33.96) * mm});
            skPoint(sketch, "E180.MirrorCS.start.orphan", {"position": v(31.63, -127.88) * mm});
            skPoint(sketch, "E181.MirrorCS.end.orphan", {"position": v(107.83, -127.88) * mm});
            skLineSegment(sketch, "E182.MirrorCS", {"start": v(87.36, -123.3) * mm, "end": v(85.6, -123.3) * mm});
            skLineSegment(sketch, "E183.MirrorCS", {"start": v(52.1, -121.53) * mm, "end": v(52.1, -123.3) * mm});
            skLineSegment(sketch, "E184.MirrorCS", {"start": v(87.36, -121.53) * mm, "end": v(87.36, -123.3) * mm});
            skLineSegment(sketch, "E185.MirrorCS", {"start": v(52.1, -119.15) * mm, "end": v(53.86, -119.15) * mm});
            skLineSegment(sketch, "E186.MirrorCS", {"start": v(53.86, -121.53) * mm, "end": v(53.86, -119.15) * mm});
            skLineSegment(sketch, "E187.MirrorCS", {"start": v(85.6, -121.53) * mm, "end": v(85.6, -119.15) * mm});
            skLineSegment(sketch, "E188.MirrorCS", {"start": v(52.1, -121.53) * mm, "end": v(53.86, -121.53) * mm});
            skLineSegment(sketch, "E189.MirrorCS", {"start": v(47.5, -119.15) * mm, "end": v(49.26, -119.15) * mm});
            skLineSegment(sketch, "E190.MirrorCS", {"start": v(47.5, -121.53) * mm, "end": v(47.5, -119.15) * mm});
            skLineSegment(sketch, "E191.MirrorCS", {"start": v(91.96, -121.53) * mm, "end": v(91.96, -119.15) * mm});
            skLineSegment(sketch, "E192.MirrorCS", {"start": v(91.96, -127.88) * mm, "end": v(91.96, -123.3) * mm});
            skLineSegment(sketch, "E193.MirrorCS", {"start": v(47.5, -121.53) * mm, "end": v(49.26, -121.53) * mm});
            skLineSegment(sketch, "E194.MirrorCS", {"start": v(91.96, -123.3) * mm, "end": v(90.2, -123.3) * mm});
            skLineSegment(sketch, "E195.MirrorCS", {"start": v(90.2, -121.53) * mm, "end": v(90.2, -123.3) * mm});
            skLineSegment(sketch, "E196.MirrorCS", {"start": v(49.26, -119.15) * mm, "end": v(49.26, -115.18) * mm});
            skLineSegment(sketch, "E197.MirrorCS", {"start": v(52.1, -119.15) * mm, "end": v(52.1, -115.18) * mm});
            skLineSegment(sketch, "E198.MirrorCS", {"start": v(47.5, -127.88) * mm, "end": v(47.5, -123.3) * mm});
            skLineSegment(sketch, "E199.MirrorCS", {"start": v(87.36, -119.15) * mm, "end": v(87.36, -115.18) * mm});
            skLineSegment(sketch, "E200.MirrorCS", {"start": v(90.2, -119.15) * mm, "end": v(90.2, -115.18) * mm});
            skLineSegment(sketch, "E201.MirrorCS", {"start": v(53.86, -127.88) * mm, "end": v(53.86, -123.3) * mm});
            skLineSegment(sketch, "E202.MirrorCS", {"start": v(85.6, -127.88) * mm, "end": v(85.6, -123.3) * mm});
            skLineSegment(sketch, "E203.MirrorCS", {"start": v(90.2, -115.18) * mm, "end": v(87.36, -115.18) * mm});
            skLineSegment(sketch, "E204.MirrorCS", {"start": v(49.26, -115.18) * mm, "end": v(52.1, -115.18) * mm});
            skLineSegment(sketch, "E205.MirrorCS", {"start": v(107.83, -127.88) * mm, "end": v(91.96, -127.88) * mm});
            skPoint(sketch, "E206.MirrorP", {"position": v(50.68, -121.53) * mm});
            skPoint(sketch, "E207.MirrorP", {"position": v(88.78, -121.53) * mm});
            skLineSegment(sketch, "E208.MirrorCS", {"start": v(53.86, -127.88) * mm, "end": v(85.6, -127.88) * mm});
            skLineSegment(sketch, "E209.MirrorCS", {"start": v(91.96, -127.88) * mm, "end": v(107.83, -127.88) * mm});
            skPoint(sketch, "E210.MirrorP", {"position": v(69.73, -127.88) * mm});
            skLineSegment(sketch, "E211", {"start": v(49.26, -121.53) * mm, "end": v(49.26, -123.3) * mm});
            skLineSegment(sketch, "E212", {"start": v(49.26, -123.3) * mm, "end": v(47.5, -123.3) * mm});
            skLineSegment(sketch, "E213", {"start": v(52.1, -123.3) * mm, "end": v(53.86, -123.3) * mm});
            skLineSegment(sketch, "E214", {"start": v(87.36, -121.53) * mm, "end": v(85.6, -121.53) * mm});
            skLineSegment(sketch, "E215", {"start": v(85.6, -119.15) * mm, "end": v(87.36, -119.15) * mm});
            skLineSegment(sketch, "E216", {"start": v(90.2, -119.15) * mm, "end": v(91.96, -119.15) * mm});
            skLineSegment(sketch, "E217", {"start": v(91.96, -121.53) * mm, "end": v(90.2, -121.53) * mm});
            skSolve(sketch);
        }
        {
            var Q0;
            Q0=makeQuery(id+"F0.imprint","IMPRINT",FACE,{"disambiguationData":[TD([[makeQuery(id+"F0.imprint","IMPRINT",EDGE,{"derivedFrom":sQuery(id+"F0.wireOp",EDGE,"E101.MirrorCS")}),1.0]])]});
            extrude(context, id + "F1", {"entities" : qUnion([Q0]), "depth" : 4.5 * mm, "offsetDistance" : 25.4 * mm});
        }
        {
            var Q0;
            Q0 = qSketchRegion(id + "F0", true);
            extrude(context, id + "F2", {"entities" : qUnion([Q0]), "operationType" : NewBodyOperationType.ADD, "depth" : 4.5 * mm, "offsetDistance" : 25.4 * mm});
        }
    });
